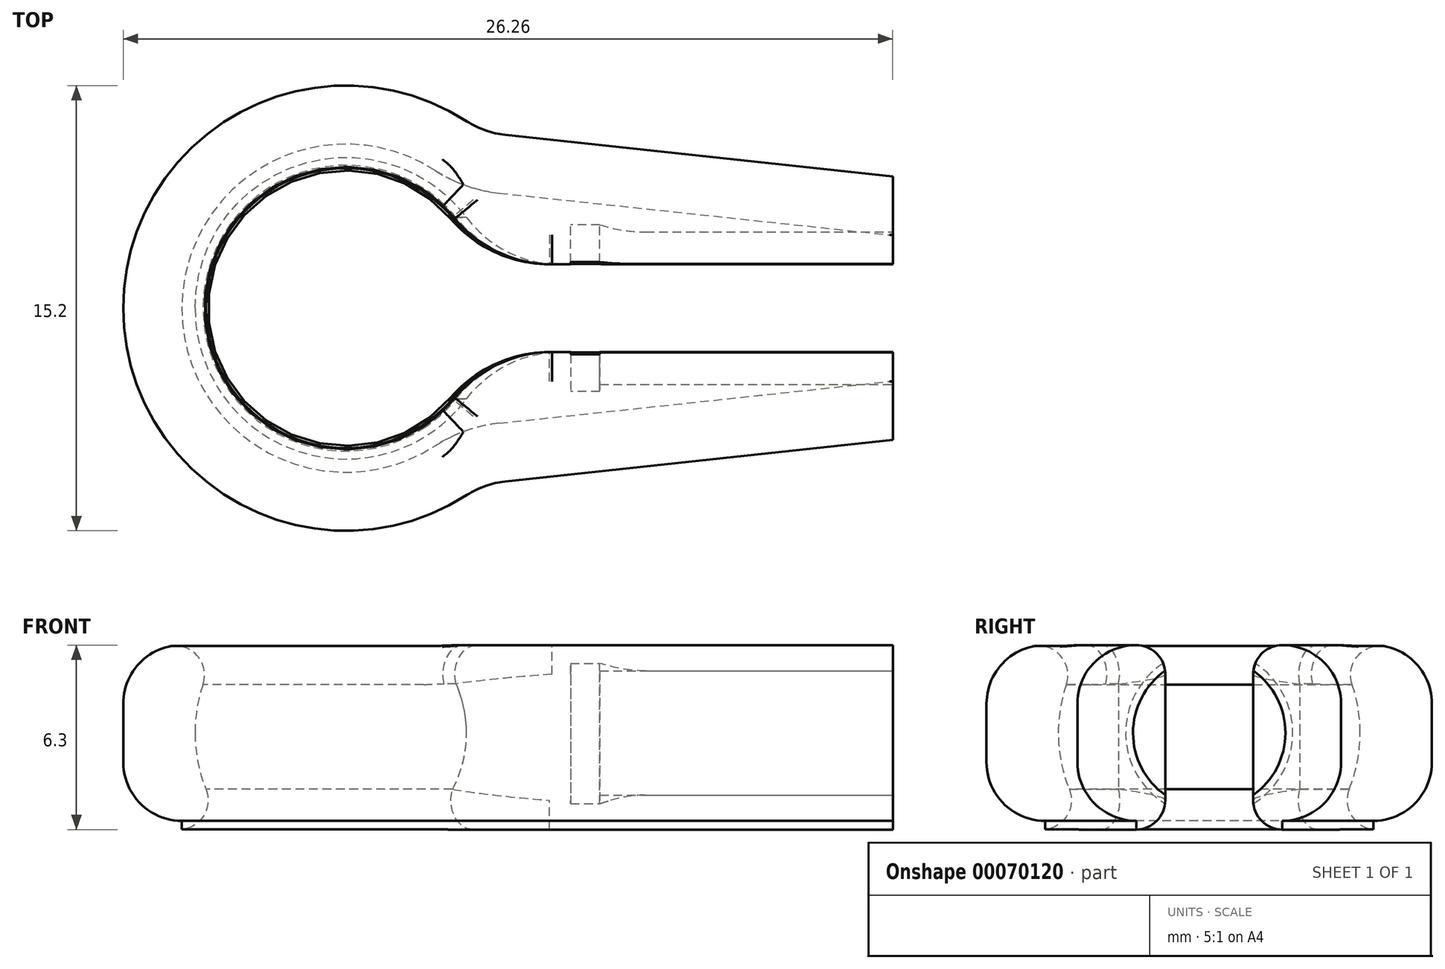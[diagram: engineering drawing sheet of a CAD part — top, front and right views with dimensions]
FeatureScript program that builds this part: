
annotation { "Feature Type Name" : "Feature", "Feature Type Description" : "" }
export const myFeature = defineFeature(function(context is Context, id is Id, definition is map)
    precondition{}
    {
        {
            assignVariable(context, id + "F0", {"name" : "ball", "anyValue" : 10});
        }
        {
            var Q0;
            Q0=qCreatedBy(makeId("Top.planeOp"),FACE);
            var sketch = newSketch(context, id + "F1", { "sketchPlane" : qUnion([Q0])});
            skCircle(sketch, "E0", {"center": v(0, 0) * mm, "radius": 5.15 * mm});
            skLineSegment(sketch, "E1", {"start": v(-13.72, 0) * mm, "end": v(11.71, 0) * mm});
            skCircle(sketch, "E2.0", {"center": v(0, 0) * mm, "radius": 7.6 * mm});
            skCircle(sketch, "E3", {"center": v(-8.05, 0) * mm, "radius": 2.9 * mm, "construction": true});
            skCircle(sketch, "E4", {"center": v(-8.05, 0) * mm, "radius": 1.4 * mm, "construction": true});
            skLineSegment(sketch, "E5.rect.bottom", {"start": v(4.66, 6) * mm, "end": v(18.66, 6) * mm});
            skLineSegment(sketch, "E5.rect.top", {"start": v(4.66, -6) * mm, "end": v(18.66, -6) * mm});
            skLineSegment(sketch, "E5.rect.left", {"start": v(4.66, 6) * mm, "end": v(4.66, -6) * mm, "construction": true});
            skLineSegment(sketch, "E5.rect.right", {"start": v(18.66, 6) * mm, "end": v(18.66, -6) * mm});
            skPoint(sketch, "E5.rect.middle", {"position": v(11.66, 0) * mm});
            skLineSegment(sketch, "E6", {"start": v(4.66, -6) * mm, "end": v(18.66, -4.5) * mm});
            skLineSegment(sketch, "E7.MirrorCS", {"start": v(4.66, 6) * mm, "end": v(18.66, 4.5) * mm});
            skSolve(sketch);
        }
        {
            var Q0;
            {var subQ0=sQuery(id+"F1.wireOp",EDGE,"E1");var subQ1=sQuery(id+"F1.wireOp",EDGE,"E0");var subQ2=makeQuery(id+"F1.imprint","INTERSECT",VERTEX,{"disambiguationData":[OD(0.0)],"derivedFrom":[subQ1,subQ0]});Q0=makeQuery(id+"F1.imprint","IMPRINT",FACE,{"disambiguationData":[TD([[makeQuery(id+"F1.imprint","IMPRINT",EDGE,{"disambiguationData":[TD([[subQ2,-1.0]])],"derivedFrom":subQ1}),-1.0]])]});}
            var Q1;
            {var subQ0=sQuery(id+"F1.wireOp",EDGE,"E1");var subQ1=sQuery(id+"F1.wireOp",EDGE,"E0");var subQ2=makeQuery(id+"F1.imprint","INTERSECT",VERTEX,{"disambiguationData":[OD(0.0)],"derivedFrom":[subQ1,subQ0]});Q1=makeQuery(id+"F1.imprint","IMPRINT",FACE,{"disambiguationData":[TD([[makeQuery(id+"F1.imprint","IMPRINT",EDGE,{"disambiguationData":[TD([[subQ2,1.0]])],"derivedFrom":subQ1}),-1.0]])]});}
            var Q2;
            {var subQ0=sQuery(id+"F1.wireOp",EDGE,"E2.0");var subQ1=sQuery(id+"F1.wireOp",EDGE,"E1");var subQ2=makeQuery(id+"F1.imprint","INTERSECT",VERTEX,{"disambiguationData":[OD(0.0)],"derivedFrom":[subQ1,subQ0]});Q2=makeQuery(id+"F1.imprint","IMPRINT",FACE,{"disambiguationData":[TD([[makeQuery(id+"F1.imprint","IMPRINT",EDGE,{"disambiguationData":[TD([[subQ2,1.0]])],"derivedFrom":subQ1}),1.0]])]});}
            var Q3;
            {var subQ0=sQuery(id+"F1.wireOp",EDGE,"E2.0");var subQ1=sQuery(id+"F1.wireOp",EDGE,"E1");var subQ2=makeQuery(id+"F1.imprint","INTERSECT",VERTEX,{"disambiguationData":[OD(0.0)],"derivedFrom":[subQ1,subQ0]});Q3=makeQuery(id+"F1.imprint","IMPRINT",FACE,{"disambiguationData":[TD([[makeQuery(id+"F1.imprint","IMPRINT",EDGE,{"disambiguationData":[TD([[subQ2,1.0]])],"derivedFrom":subQ1}),-1.0]])]});}
            var Q4;
            {var subQ0=sQuery(id+"F1.wireOp",EDGE,"E4");var subQ1=sQuery(id+"F1.wireOp",EDGE,"E1");var subQ2=makeQuery(id+"F1.imprint","INTERSECT",VERTEX,{"disambiguationData":[OD(1.0)],"derivedFrom":[subQ1,subQ0]});Q4=makeQuery(id+"F1.imprint","IMPRINT",FACE,{"disambiguationData":[TD([[makeQuery(id+"F1.imprint","IMPRINT",EDGE,{"disambiguationData":[TD([[subQ2,-1.0]])],"derivedFrom":subQ1}),1.0]])]});}
            var Q5;
            {var subQ0=sQuery(id+"F1.wireOp",EDGE,"E4");var subQ1=sQuery(id+"F1.wireOp",EDGE,"E1");var subQ2=makeQuery(id+"F1.imprint","INTERSECT",VERTEX,{"disambiguationData":[OD(1.0)],"derivedFrom":[subQ1,subQ0]});Q5=makeQuery(id+"F1.imprint","IMPRINT",FACE,{"disambiguationData":[TD([[makeQuery(id+"F1.imprint","IMPRINT",EDGE,{"disambiguationData":[TD([[subQ2,-1.0]])],"derivedFrom":subQ1}),-1.0]])]});}
            var Q6;
            {var subQ0=sQuery(id+"F1.wireOp",EDGE,"E1");var subQ1=sQuery(id+"F1.wireOp",EDGE,"E0");var subQ2=makeQuery(id+"F1.imprint","INTERSECT",VERTEX,{"disambiguationData":[OD(0.0)],"derivedFrom":[subQ1,subQ0]});Q6=makeQuery(id+"F1.imprint","IMPRINT",FACE,{"disambiguationData":[TD([[makeQuery(id+"F1.imprint","IMPRINT",EDGE,{"disambiguationData":[TD([[subQ2,1.0]])],"derivedFrom":subQ1}),1.0]])]});}
            var Q7;
            {var subQ0=sQuery(id+"F1.wireOp",EDGE,"E1");var subQ1=sQuery(id+"F1.wireOp",EDGE,"E0");var subQ2=makeQuery(id+"F1.imprint","INTERSECT",VERTEX,{"disambiguationData":[OD(0.0)],"derivedFrom":[subQ1,subQ0]});Q7=makeQuery(id+"F1.imprint","IMPRINT",FACE,{"disambiguationData":[TD([[makeQuery(id+"F1.imprint","IMPRINT",EDGE,{"disambiguationData":[TD([[subQ2,-1.0]])],"derivedFrom":subQ1}),1.0]])]});}
            var Q8;
            {var subQ0=sQuery(id+"F1.wireOp",EDGE,"E6");Q8=makeQuery(id+"F1.imprint","IMPRINT",FACE,{"disambiguationData":[TD([[makeQuery(id+"F1.imprint","IMPRINT",EDGE,{"derivedFrom":subQ0}),1.0]])]});}
            extrude(context, id + "F2", {"entities" : qUnion([Q0, Q1, Q2, Q3, Q4, Q5, Q6, Q7, Q8]), "endBound" : BoundingType.SYMMETRIC, "depth" : (getVariable(context, 'ball') / 2 + 1) * mm});
        }
        {
            var Q0;
            {var subQ0=sQuery(id+"F1.wireOp",EDGE,"E1");var subQ1=sQuery(id+"F1.wireOp",EDGE,"E0");var subQ2=makeQuery(id+"F1.imprint","INTERSECT",VERTEX,{"disambiguationData":[OD(0.0)],"derivedFrom":[subQ1,subQ0]});Q0=makeQuery(id+"F1.imprint","IMPRINT",FACE,{"disambiguationData":[TD([[makeQuery(id+"F1.imprint","IMPRINT",EDGE,{"disambiguationData":[TD([[subQ2,-1.0]])],"derivedFrom":subQ1}),1.0]])]});}
            var Q1;
            Q1=sQuery(id+"F1.wireOp",EDGE,"E1");
            revolve(context, id + "F3", {"operationType" : NewBodyOperationType.REMOVE, "entities" : qUnion([Q0]), "axis" : qUnion([Q1]), "revolveType" : RevolveType.FULL, "oppositeDirection" : true});
        }
        {
            var Q0;
            Q0=makeQuery(id+"F2.opExtrude","SWEPT_FACE",FACE,{"disambiguationData":[OSD([sQuery(id+"F1.wireOp",EDGE,"E5.rect.right")])]});
            var sketch = newSketch(context, id + "F4", { "sketchPlane" : qUnion([Q0])});
            skCircle(sketch, "E8", {"center": v(0, 0) * mm, "radius": 2.6 * mm});
            skLineSegment(sketch, "E9.bottom", {"start": v(-1.5, 3) * mm, "end": v(1.5, 3) * mm});
            skLineSegment(sketch, "E9.top", {"start": v(-1.5, -3) * mm, "end": v(1.5, -3) * mm});
            skLineSegment(sketch, "E9.left", {"start": v(-1.5, 3) * mm, "end": v(-1.5, -3) * mm});
            skLineSegment(sketch, "E9.right", {"start": v(1.5, 3) * mm, "end": v(1.5, -3) * mm});
            skSolve(sketch);
        }
        {
            var Q0;
            Q0=makeQuery(id+"F2.opExtrude","CAP_FACE",FACE,{"disambiguationData":[OSD([sQuery(id+"F1.wireOp",EDGE,"E2.0"),sQuery(id+"F1.wireOp",EDGE,"E4"),sQuery(id+"F1.wireOp",EDGE,"E5.rect.bottom"),sQuery(id+"F1.wireOp",EDGE,"E5.rect.top"),sQuery(id+"F1.wireOp",EDGE,"E5.rect.right")])],"isStart":false});
            var sketch = newSketch(context, id + "F5", { "sketchPlane" : qUnion([Q0])});
            skPoint(sketch, "E10.0", {"position": v(0, 0) * mm});
            skCircle(sketch, "E11", {"center": v(0, 0) * mm, "radius": 5.8 * mm, "construction": true});
            skCircle(sketch, "E12.0", {"center": v(0, 0) * mm, "radius": 6 * mm, "construction": true});
            skLineSegment(sketch, "E13.rect.bottom", {"start": v(-5.78, 0.5) * mm, "end": v(0.17, 0.5) * mm, "construction": true});
            skLineSegment(sketch, "E13.rect.top", {"start": v(-5.78, -0.5) * mm, "end": v(0.17, -0.5) * mm, "construction": true});
            skLineSegment(sketch, "E13.rect.left", {"start": v(-5.78, 0.5) * mm, "end": v(-5.78, -0.5) * mm, "construction": true});
            skLineSegment(sketch, "E13.rect.right", {"start": v(0.17, 0.5) * mm, "end": v(0.17, -0.5) * mm, "construction": true});
            skPoint(sketch, "E13.rect.middle", {"position": v(-2.8, 0) * mm});
            skLineSegment(sketch, "E14.bottom", {"start": v(19.76, 1.5) * mm, "end": v(-4.86, 1.5) * mm});
            skLineSegment(sketch, "E14.top", {"start": v(19.76, -1.5) * mm, "end": v(-4.86, -1.5) * mm});
            skLineSegment(sketch, "E14.left", {"start": v(19.76, 1.5) * mm, "end": v(19.76, -1.5) * mm});
            skLineSegment(sketch, "E14.right", {"start": v(-4.86, 1.5) * mm, "end": v(-4.86, -1.5) * mm});
            skPoint(sketch, "E14.middle", {"position": v(7.45, 0) * mm});
            skSolve(sketch);
        }
        {
            var Q0;
            {var subQ0=sQuery(id+"F5.wireOp",EDGE,"E14.bottom");var subQ1=makeQuery(id+"F3.boolean.opBoolean","INTERSECT",EDGE,{"derivedFrom":[makeQuery(id+"F2.opExtrude","CAP_FACE",FACE,{"disambiguationData":[OSD([sQuery(id+"F1.wireOp",EDGE,"E2.0"),sQuery(id+"F1.wireOp",EDGE,"E5.rect.bottom"),sQuery(id+"F1.wireOp",EDGE,"E5.rect.top"),sQuery(id+"F1.wireOp",EDGE,"E5.rect.right")])],"isStart":false}),makeQuery(id+"F3.opRevolve","SWEPT_FACE",FACE,{"disambiguationData":[OSD([sQuery(id+"F1.wireOp",EDGE,"E0")])]})]});var subQ2=makeQuery(id+"F5.imprint","INTERSECT",VERTEX,{"disambiguationData":[OD(0.0)],"derivedFrom":[subQ1,subQ0]});Q0=makeQuery(id+"F5.imprint","IMPRINT",FACE,{"disambiguationData":[TD([[makeQuery(id+"F5.imprint","IMPRINT",EDGE,{"disambiguationData":[TD([[subQ2,-1.0]])],"derivedFrom":subQ0}),1.0]])]});}
            var Q1;
            {var subQ0=sQuery(id+"F5.wireOp",EDGE,"E14.bottom");var subQ1=sQuery(id+"F1.wireOp",EDGE,"E5.rect.right");var subQ2=makeQuery(id+"F2.opExtrude","CAP_EDGE",EDGE,{"disambiguationData":[OSD([subQ1])],"isStart":false});var subQ3=makeQuery(id+"F5.imprint","INTERSECT",VERTEX,{"derivedFrom":[subQ2,subQ0]});Q1=makeQuery(id+"F5.imprint","IMPRINT",FACE,{"disambiguationData":[TD([[makeQuery(id+"F5.imprint","IMPRINT",EDGE,{"disambiguationData":[TD([[subQ3,-1.0]])],"derivedFrom":subQ2}),-1.0]])]});}
            extrude(context, id + "F6", {"entities" : qUnion([Q0, Q1]), "operationType" : NewBodyOperationType.REMOVE, "oppositeDirection" : true, "depth" : 25 * mm});
        }
        {
            var Q0;
            {var subQ0=sQuery(id+"F4.wireOp",EDGE,"E9.right");var subQ1=sQuery(id+"F4.wireOp",EDGE,"E8");var subQ2=makeQuery(id+"F4.imprint","INTERSECT",VERTEX,{"disambiguationData":[OD(0.0)],"derivedFrom":[subQ1,subQ0]});Q0=makeQuery(id+"F4.imprint","IMPRINT",FACE,{"disambiguationData":[TD([[makeQuery(id+"F4.imprint","IMPRINT",EDGE,{"disambiguationData":[TD([[subQ2,1.0]])],"derivedFrom":subQ1}),1.0]])]});}
            var Q1;
            {var subQ0=sQuery(id+"F4.wireOp",EDGE,"E9.left");var subQ1=sQuery(id+"F4.wireOp",EDGE,"E8");var subQ2=makeQuery(id+"F4.imprint","INTERSECT",VERTEX,{"disambiguationData":[OD(0.0)],"derivedFrom":[subQ1,subQ0]});Q1=makeQuery(id+"F4.imprint","IMPRINT",FACE,{"disambiguationData":[TD([[makeQuery(id+"F4.imprint","IMPRINT",EDGE,{"disambiguationData":[TD([[subQ2,-1.0]])],"derivedFrom":subQ1}),1.0]])]});}
            extrude(context, id + "F7", {"entities" : qUnion([Q0, Q1]), "operationType" : NewBodyOperationType.REMOVE, "oppositeDirection" : true, "depth" : 11 * mm});
        }
        {
            var Q0;
            Q0=makeQuery(id+"F2.opExtrude","SWEPT_EDGE",EDGE,{"disambiguationData":[OSD([sQuery(id+"F1.wireOp",EDGE,"E2.0"),sQuery(id+"F1.wireOp",EDGE,"E5.rect.top")])]});
            var Q1;
            Q1=makeQuery(id+"F2.opExtrude","SWEPT_EDGE",EDGE,{"disambiguationData":[OSD([sQuery(id+"F1.wireOp",EDGE,"E2.0"),sQuery(id+"F1.wireOp",EDGE,"E5.rect.bottom")])]});
            fillet(context, id + "F8", {"entities" : qUnion([Q0, Q1]), "radius" : 3 * mm, "tangentPropagation" : true, "allowEdgeOverflow" : false});
        }
        {
            var Q0;
            Q0=makeQuery(id+"F2.opExtrude","CAP_EDGE",EDGE,{"disambiguationData":[OSD([sQuery(id+"F1.wireOp",EDGE,"E2.0")])],"isStart":true});
            var Q1;
            Q1=makeQuery(id+"F2.opExtrude","CAP_EDGE",EDGE,{"disambiguationData":[OSD([sQuery(id+"F1.wireOp",EDGE,"E2.0")])],"isStart":false});
            fillet(context, id + "F9", {"entities" : qUnion([Q0, Q1]), "radius" : 2 * mm, "tangentPropagation" : true, "allowEdgeOverflow" : false});
        }
        {
            var Q0;
            {var subQ0=sQuery(id+"F4.wireOp",EDGE,"E8");var subQ1=sQuery(id+"F1.wireOp",EDGE,"E5.rect.right");Q0=makeQuery(id+"F7.boolean.opBoolean","INTERSECT",EDGE,{"derivedFrom":[makeQuery(id+"F3.boolean.opBoolean","COPY",FACE,{"derivedFrom":makeQuery(id+"F3.opRevolve","SWEPT_FACE",FACE,{"disambiguationData":[OSD([sQuery(id+"F1.wireOp",EDGE,"E0")])]})}),makeQuery(id+"F7.opExtrude","SWEPT_FACE",FACE,{"disambiguationData":[OSD([subQ0]),TDD([makeQuery(id+"F4.imprint","IMPRINT",EDGE,{"disambiguationData":[TD([[makeQuery(id+"F4.imprint","INTERSECT",VERTEX,{"disambiguationData":[OD(1.0)],"derivedFrom":[makeQuery(id+"F2.opExtrude","CAP_EDGE",EDGE,{"disambiguationData":[OSD([subQ1])],"isStart":false}),subQ0]}),1.0]])],"derivedFrom":subQ0})])]})]});}
            var Q1;
            {var subQ0=sQuery(id+"F4.wireOp",EDGE,"E8");var subQ1=sQuery(id+"F1.wireOp",EDGE,"E5.rect.right");Q1=makeQuery(id+"F7.boolean.opBoolean","INTERSECT",EDGE,{"derivedFrom":[makeQuery(id+"F3.boolean.opBoolean","COPY",FACE,{"derivedFrom":makeQuery(id+"F3.opRevolve","SWEPT_FACE",FACE,{"disambiguationData":[OSD([sQuery(id+"F1.wireOp",EDGE,"E0")])]})}),makeQuery(id+"F7.opExtrude","SWEPT_FACE",FACE,{"disambiguationData":[OSD([subQ0]),TDD([makeQuery(id+"F4.imprint","IMPRINT",EDGE,{"disambiguationData":[TD([[makeQuery(id+"F4.imprint","INTERSECT",VERTEX,{"disambiguationData":[OD(0.0)],"derivedFrom":[makeQuery(id+"F2.opExtrude","CAP_EDGE",EDGE,{"disambiguationData":[OSD([subQ1])],"isStart":false}),subQ0]}),-1.0]])],"derivedFrom":subQ0})])]})]});}
            var Q2;
            {var subQ0=makeQuery(id+"F3.boolean.opBoolean","COPY",FACE,{"derivedFrom":makeQuery(id+"F3.opRevolve","SWEPT_FACE",FACE,{"disambiguationData":[OSD([sQuery(id+"F1.wireOp",EDGE,"E0")])]})});var subQ1=makeQuery(id+"F6.opExtrude","SWEPT_FACE",FACE,{"disambiguationData":[OSD([sQuery(id+"F5.wireOp",EDGE,"E14.top")])]});Q2=makeQuery(id+"F7.boolean.opBoolean","SPLIT",EDGE,{"disambiguationData":[TD([makeQuery(id+"F2.opExtrude","CAP_FACE",FACE,{"disambiguationData":[OSD([sQuery(id+"F1.wireOp",EDGE,"E2.0"),sQuery(id+"F1.wireOp",EDGE,"E5.rect.right"),sQuery(id+"F1.wireOp",EDGE,"E6"),sQuery(id+"F1.wireOp",EDGE,"E7.MirrorCS")])],"isStart":false})])],"derivedFrom":makeQuery(id+"F6.boolean.opBoolean","INTERSECT",EDGE,{"derivedFrom":[subQ0,subQ1]})});}
            var Q3;
            {var subQ0=makeQuery(id+"F3.boolean.opBoolean","COPY",FACE,{"derivedFrom":makeQuery(id+"F3.opRevolve","SWEPT_FACE",FACE,{"disambiguationData":[OSD([sQuery(id+"F1.wireOp",EDGE,"E0")])]})});var subQ1=makeQuery(id+"F6.opExtrude","SWEPT_FACE",FACE,{"disambiguationData":[OSD([sQuery(id+"F5.wireOp",EDGE,"E14.top")])]});Q3=makeQuery(id+"F7.boolean.opBoolean","SPLIT",EDGE,{"disambiguationData":[TD([makeQuery(id+"F2.opExtrude","CAP_FACE",FACE,{"disambiguationData":[OSD([sQuery(id+"F1.wireOp",EDGE,"E2.0"),sQuery(id+"F1.wireOp",EDGE,"E5.rect.right"),sQuery(id+"F1.wireOp",EDGE,"E6"),sQuery(id+"F1.wireOp",EDGE,"E7.MirrorCS")])],"isStart":true})])],"derivedFrom":makeQuery(id+"F6.boolean.opBoolean","INTERSECT",EDGE,{"derivedFrom":[subQ0,subQ1]})});}
            var Q4;
            {var subQ0=makeQuery(id+"F3.boolean.opBoolean","COPY",FACE,{"derivedFrom":makeQuery(id+"F3.opRevolve","SWEPT_FACE",FACE,{"disambiguationData":[OSD([sQuery(id+"F1.wireOp",EDGE,"E0")])]})});var subQ1=makeQuery(id+"F6.opExtrude","SWEPT_FACE",FACE,{"disambiguationData":[OSD([sQuery(id+"F5.wireOp",EDGE,"E14.bottom")])]});Q4=makeQuery(id+"F7.boolean.opBoolean","SPLIT",EDGE,{"disambiguationData":[TD([makeQuery(id+"F2.opExtrude","CAP_FACE",FACE,{"disambiguationData":[OSD([sQuery(id+"F1.wireOp",EDGE,"E2.0"),sQuery(id+"F1.wireOp",EDGE,"E5.rect.right"),sQuery(id+"F1.wireOp",EDGE,"E6"),sQuery(id+"F1.wireOp",EDGE,"E7.MirrorCS")])],"isStart":false})])],"derivedFrom":makeQuery(id+"F6.boolean.opBoolean","INTERSECT",EDGE,{"derivedFrom":[subQ0,subQ1]})});}
            var Q5;
            {var subQ0=makeQuery(id+"F3.boolean.opBoolean","COPY",FACE,{"derivedFrom":makeQuery(id+"F3.opRevolve","SWEPT_FACE",FACE,{"disambiguationData":[OSD([sQuery(id+"F1.wireOp",EDGE,"E0")])]})});var subQ1=makeQuery(id+"F6.opExtrude","SWEPT_FACE",FACE,{"disambiguationData":[OSD([sQuery(id+"F5.wireOp",EDGE,"E14.bottom")])]});Q5=makeQuery(id+"F7.boolean.opBoolean","SPLIT",EDGE,{"disambiguationData":[TD([makeQuery(id+"F2.opExtrude","CAP_FACE",FACE,{"disambiguationData":[OSD([sQuery(id+"F1.wireOp",EDGE,"E2.0"),sQuery(id+"F1.wireOp",EDGE,"E5.rect.right"),sQuery(id+"F1.wireOp",EDGE,"E6"),sQuery(id+"F1.wireOp",EDGE,"E7.MirrorCS")])],"isStart":true})])],"derivedFrom":makeQuery(id+"F6.boolean.opBoolean","INTERSECT",EDGE,{"derivedFrom":[subQ0,subQ1]})});}
            fillet(context, id + "F10", {"entities" : qUnion([Q0, Q1, Q2, Q3, Q4, Q5]), "radius" : 4 * mm, "tangentPropagation" : true, "allowEdgeOverflow" : false});
        }
        {
            var Q0;
            Q0=makeQuery(id+"F7.boolean.opBoolean","COPY",FACE,{"derivedFrom":makeQuery(id+"F7.opExtrude","CAP_FACE",FACE,{"disambiguationData":[OSD([sQuery(id+"F4.wireOp",EDGE,"E8"),sQuery(id+"F4.wireOp",EDGE,"E9.left")])],"isStart":false})});
            var sketch = newSketch(context, id + "F11", { "sketchPlane" : qUnion([Q0])});
            skCircle(sketch, "E15", {"center": v(0, 0) * mm, "radius": 2.85 * mm});
            skSolve(sketch);
        }
        {
            var Q0;
            Q0=makeQuery(id+"F11.imprint","IMPRINT",FACE,{"disambiguationData":[TD([[makeQuery(id+"F11.imprint","IMPRINT",EDGE,{"derivedFrom":sQuery(id+"F11.wireOp",EDGE,"E15")}),1.0]])]});
            var Q1;
            {var subQ1=sQuery(id+"F4.wireOp",EDGE,"jmoEVadG-jTNw-YKId-jH0M-iueLH38AlG3W");Q1=makeQuery(id+"F11.imprint","IMPRINT",FACE,{"disambiguationData":[TD([[makeQuery(id+"F11.imprint","IMPRINT",EDGE,{"derivedFrom":makeQuery(id+"FZhEncpM2523xPu_1.boolean.opBoolean","COPY",EDGE,{"disambiguationData":[OD(1.0)],"derivedFrom":makeQuery(id+"FZhEncpM2523xPu_1.opExtrude","CAP_EDGE",EDGE,{"disambiguationData":[OSD([subQ1])],"isStart":false})})}),-1.0]])]});}
            extrude(context, id + "F12", {"entities" : qUnion([Q0, Q1]), "operationType" : NewBodyOperationType.REMOVE, "depth" : 1 * mm});
        }
        {
            var Q0;
            Q0=makeQuery(id+"F12.boolean.opBoolean","COPY",EDGE,{"derivedFrom":makeQuery(id+"F12.opExtrude","CAP_EDGE",EDGE,{"disambiguationData":[OSD([sQuery(id+"F4.wireOp",EDGE,"E8")])],"isStart":false})});
            var Q1;
            {var subQ0=sQuery(id+"F4.wireOp",EDGE,"E8");var subQ1=sQuery(id+"F4.wireOp",EDGE,"E9.right");Q1=makeQuery(id+"F12.boolean.opBoolean","INTERSECT",EDGE,{"derivedFrom":[makeQuery(id+"F7.boolean.opBoolean","COPY",FACE,{"derivedFrom":makeQuery(id+"F7.opExtrude","SWEPT_FACE",FACE,{"disambiguationData":[OSD([subQ0]),TDD([makeQuery(id+"F4.imprint","IMPRINT",EDGE,{"disambiguationData":[TD([[makeQuery(id+"F4.imprint","INTERSECT",VERTEX,{"disambiguationData":[OD(0.0)],"derivedFrom":[subQ0,subQ1]}),1.0]])],"derivedFrom":subQ0})])]})}),makeQuery(id+"F12.opExtrude","CAP_FACE",FACE,{"disambiguationData":[OSD([subQ0,sQuery(id+"F4.wireOp",EDGE,"E9.left"),sQuery(id+"F11.wireOp",EDGE,"E15")])],"isStart":false})]});}
            fillet(context, id + "F13", {"entities" : qUnion([Q0, Q1]), "radius" : 5 * mm, "tangentPropagation" : true, "allowEdgeOverflow" : false});
        }
        {
            var Q0;
            Q0=makeQuery(id+"F2.opExtrude","CAP_FACE",FACE,{"disambiguationData":[OSD([sQuery(id+"F1.wireOp",EDGE,"E2.0"),sQuery(id+"F1.wireOp",EDGE,"E5.rect.right"),sQuery(id+"F1.wireOp",EDGE,"E6"),sQuery(id+"F1.wireOp",EDGE,"E7.MirrorCS")])],"isStart":true});
            var sketch = newSketch(context, id + "F14", { "sketchPlane" : qUnion([Q0])});
            skLineSegment(sketch, "E16.0", {"start": v(19.66, -3.32) * mm, "end": v(19.66, -0.5) * mm});
            skLineSegment(sketch, "E16.1", {"start": v(6.67, 0.5) * mm, "end": v(19.66, 0.5) * mm});
            skFitSpline(sketch, "E16.2", {"points": [v(2.54, 1.92) * mm, v(2.63, 1.8) * mm, v(2.83, 1.58) * mm, v(3.25, 1.2) * mm, v(3.85, 0.84) * mm, v(4.63, 0.57) * mm, v(5.18, 0.5) * mm, v(5.47, 0.5) * mm]});
            skArc(sketch, "E16.3", {"start": v(2.14, 2.36) * mm, "mid": v(-3.19, 0) * mm, "end": v(2.14, -2.36) * mm});
            skFitSpline(sketch, "E16.4", {"points": [v(5.47, -0.5) * mm, v(4.9, -0.5) * mm, v(4.09, -0.7) * mm, v(3.14, -1.27) * mm, v(2.73, -1.68) * mm, v(2.54, -1.92) * mm]});
            skLineSegment(sketch, "E16.5", {"start": v(19.66, 0.5) * mm, "end": v(19.66, 3.32) * mm});
            skLineSegment(sketch, "E16.6", {"start": v(19.66, -0.5) * mm, "end": v(6.67, -0.5) * mm});
            skLineSegment(sketch, "E16.7", {"start": v(19.66, 3.32) * mm, "end": v(5.33, 5.88) * mm});
            skArc(sketch, "E16.8", {"start": v(5.33, 5.88) * mm, "mid": v(4.74, 6.05) * mm, "end": v(4.2, 6.33) * mm});
            skArc(sketch, "E16.9", {"start": v(4.2, 6.33) * mm, "mid": v(-7.6, 0) * mm, "end": v(4.2, -6.33) * mm});
            skArc(sketch, "E16.10", {"start": v(4.2, -6.33) * mm, "mid": v(4.74, -6.05) * mm, "end": v(5.33, -5.88) * mm});
            skLineSegment(sketch, "E16.11", {"start": v(5.33, -5.88) * mm, "end": v(19.66, -3.32) * mm});
            skLineSegment(sketch, "E17", {"start": v(18.66, -3.5) * mm, "end": v(18.66, 3.5) * mm});
            skPoint(sketch, "E17.endSnap0", {"position": v(18.66, 2) * mm});
            skSolve(sketch);
        }
        {
            var Q0;
            {var subQ0=sQuery(id+"F1.wireOp",EDGE,"E7.MirrorCS");var subQ1=sQuery(id+"F1.wireOp",EDGE,"E6");var subQ2=sQuery(id+"F1.wireOp",EDGE,"E2.0");var subQ3=makeQuery(id+"F2.opExtrude","CAP_FACE",FACE,{"disambiguationData":[OSD([subQ2,sQuery(id+"F1.wireOp",EDGE,"E5.rect.right"),subQ1,subQ0])],"isStart":true});var subQ4=subQ3;var subQ5=subQ4;var subQ6=subQ5;Q0=makeQuery(id+"F14.imprint","IMPRINT",FACE,{"disambiguationData":[TD([[makeQuery(id+"F14.imprint","IMPRINT",EDGE,{"derivedFrom":makeQuery(id+"F9.opFillet","BLEND_EDGE",EDGE,{"blendedFrom":[makeQuery(id+"F2.opExtrude","CAP_EDGE",EDGE,{"disambiguationData":[OSD([subQ2])],"isStart":true}),subQ6],"blendedInto":[subQ6]})}),1.0]])]});}
            var Q1;
            {var subQ13=sQuery(id+"F14.wireOp",EDGE,"E16.8");Q1=makeQuery(id+"F14.imprint","IMPRINT",FACE,{"disambiguationData":[TD([[makeQuery(id+"F14.imprint","IMPRINT",EDGE,{"derivedFrom":subQ13}),1.0]])]});}
            extrude(context, id + "F15", {"entities" : qUnion([Q0, Q1]), "operationType" : NewBodyOperationType.ADD, "depth" : 0.3 * mm});
        }
        {
            var Q0;
            Q0=makeQuery(id+"F3.boolean.opBoolean","INTERSECT",EDGE,{"derivedFrom":[makeQuery(id+"F2.opExtrude","CAP_FACE",FACE,{"disambiguationData":[OSD([sQuery(id+"F1.wireOp",EDGE,"E2.0"),sQuery(id+"F1.wireOp",EDGE,"E5.rect.right"),sQuery(id+"F1.wireOp",EDGE,"E6"),sQuery(id+"F1.wireOp",EDGE,"E7.MirrorCS")])],"isStart":false}),makeQuery(id+"F3.opRevolve","SWEPT_FACE",FACE,{"disambiguationData":[OSD([sQuery(id+"F1.wireOp",EDGE,"E0")])]})]});
            var Q1;
            Q1=makeQuery(id+"F15.opExtrude","CAP_EDGE",EDGE,{"disambiguationData":[OSD([sQuery(id+"F1.wireOp",EDGE,"E0"),sQuery(id+"F1.wireOp",EDGE,"E2.0"),sQuery(id+"F1.wireOp",EDGE,"E5.rect.right"),sQuery(id+"F1.wireOp",EDGE,"E6"),sQuery(id+"F1.wireOp",EDGE,"E7.MirrorCS")])],"isStart":false});
            fillet(context, id + "F16", {"entities" : qUnion([Q0, Q1]), "radius" : 1 * mm, "tangentPropagation" : true, "allowEdgeOverflow" : false});
        }
    });
